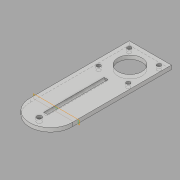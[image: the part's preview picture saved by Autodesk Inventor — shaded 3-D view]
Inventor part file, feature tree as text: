
AUTODESK INVENTOR PART (.ipt)
format: ipt  version: 2017 (Build 210142000, 142)  size: 109,568 bytes
history: native  units: mm
features: extrude x5, sketch x5, plane x1
ambient origin geometry x8: Origin, YZ Plane, XZ Plane, XY Plane, X Axis, Y Axis, Z Axis, Center Point
bodies: Solid1 (feature_tree)
feature tree (11):
  extrude  "Extrusion1"  Depth=4.0mm TaperAngle=0.0deg
  extrude  "Extrusion2"  [1 undecoded]
  extrude  "Extrusion3"  Depth=4.0mm TaperAngle=0.0deg
  plane  "Work Plane1"
  extrude  "Extrusion4"  Depth=4.0mm TaperAngle=0.0deg
  extrude  "Extrusion5"  Depth=5.0mm
  sketch  "Sketch1"  dims[d0=4.0mm d1=0.0mm d9=4.0mm d10=0.0mm]
  sketch  "Sketch2"  dims[d11=4.0mm d12=0.0mm d13=-60.0mm]
  sketch  "Sketch3"  dims[d14=4.0mm d15=51.75mm d16=11.25mm d17=0.0mm d18=0.0mm]
  sketch  "Sketch4"  dims[d19=25.0mm d20=4.0mm d21=0.0mm]
  sketch  "Sketch5"  dims[d22=44.0mm d24=5.0mm]
note: 1 required parameter value undecoded (feature->parameter linkage not recoverable at this tier; creation-order binding heuristic only, values carry confidence <= 0.55)
